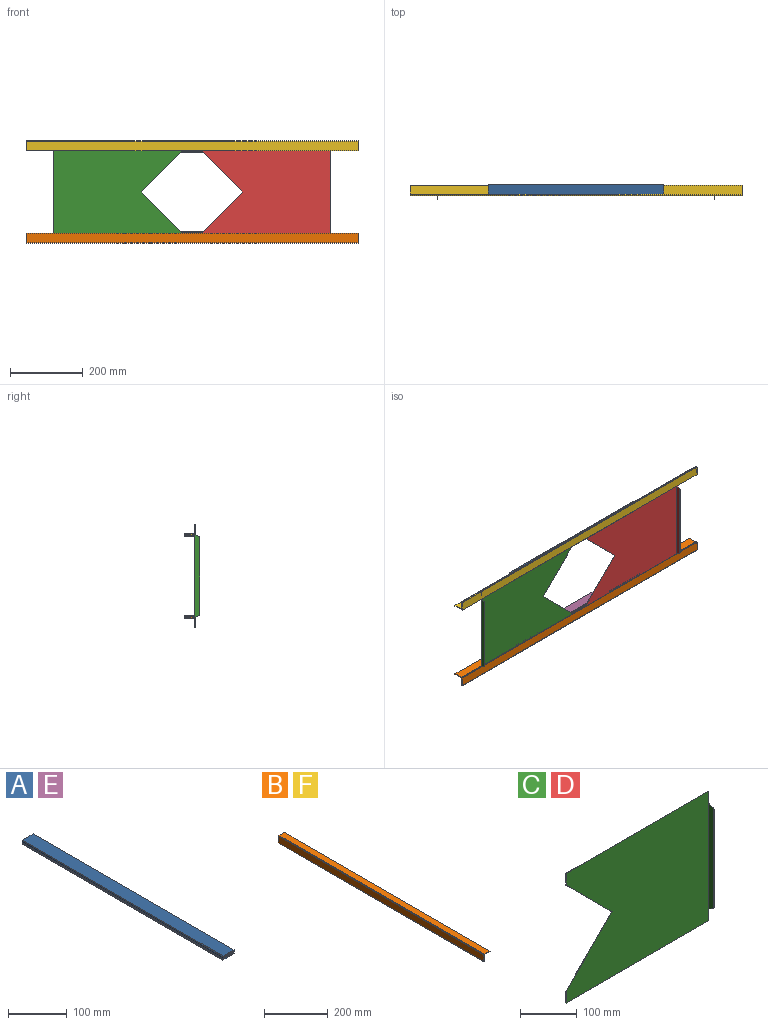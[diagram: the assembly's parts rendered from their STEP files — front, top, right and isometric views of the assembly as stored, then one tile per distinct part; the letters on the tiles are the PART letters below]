
ASSEMBLY  parts=6 mates=13
PART A: 18 faces, bbox 27x482.6x8 mm
  f0: plane 482.6x1.6mm, normal (-1,0,0), area 772.3mm2, adj f1,f11,f12,f13
  f1: plane 482.6x26.24mm, normal (0,0,-1), area 12662.6mm2, adj f0,f12,f13,f17
  f2: plane 482.6x3.28mm, normal (1,0,0), area 1581.3mm2, adj f12,f13,f16,f17
  f3: plane 482.6x24.64mm, normal (0,0,1), area 11890.3mm2, adj f4,f12,f13,f16
  f4: plane 482.6x1.6mm, normal (1,0,0), area 772.3mm2, adj f3,f5,f12,f13
  f5: plane 482.6x25.4mm, normal (0,0,-1), area 12258mm2, adj f4,f6,f12,f13
  f6: plane 482.6x1.6mm, normal (1,0,0), area 772.3mm2, adj f5,f7,f12,f13
  f7: plane 482.6x26.24mm, normal (0,0,1), area 12662.6mm2, adj f6,f12,f13,f14
  f8: plane 482.6x3.28mm, normal (-1,0,0), area 1581.3mm2, adj f12,f13,f14,f15
  f9: plane 482.6x24.64mm, normal (0,0,-1), area 11890.3mm2, adj f10,f12,f13,f15
  f10: plane 482.6x1.6mm, normal (-1,0,0), area 772.3mm2, adj f9,f11,f12,f13
  f11: plane 482.6x25.4mm, normal (0,0,1), area 12258mm2, adj f0,f10,f12,f13
  f12: plane 27x8mm, normal (0,-1,0), area 134.2mm2, adj f0,f1,f2,f3,f4,f5,f6,f7
  f13: plane 27x8mm, normal (0,1,0), area 134.2mm2, adj f0,f1,f2,f3,f4,f5,f6,f7
  f14: cylinder r=0.76mm len=482.6mm, axis (0,1,0), area 577.6mm2, adj f7,f8,f12,f13
  f15: cylinder r=0.76mm len=482.6mm, axis (0,1,0), area 577.6mm2, adj f8,f9,f12,f13
  f16: cylinder r=0.76mm len=482.6mm, axis (0,1,0), area 577.6mm2, adj f2,f3,f12,f13
  f17: cylinder r=0.76mm len=482.6mm, axis (0,1,0), area 577.6mm2, adj f1,f2,f12,f13
PART B: 15 faces, bbox 28.3x914.4x27 mm
  f0: plane 914.4x1.59mm, normal (1,0,0), area 1451.6mm2, adj f1,f9,f10,f11
  f1: plane 914.4x23.88mm, normal (0,0,1), area 21832.2mm2, adj f0,f10,f11,f14
  f2: plane 914.4x23.88mm, normal (-1,0,0), area 21832.2mm2, adj f3,f10,f11,f14
  f3: plane 914.4x1.27mm, normal (0,0,1), area 1161.3mm2, adj f2,f4,f10,f11
  f4: plane 914.4x25.4mm, normal (1,0,0), area 23225.8mm2, adj f3,f5,f10,f11
  f5: plane 914.4x1.59mm, normal (0,0,1), area 1451.6mm2, adj f4,f6,f10,f11
  f6: plane 914.4x25.46mm, normal (-1,0,0), area 23283.8mm2, adj f5,f10,f11,f13
  f7: plane 914.4x1.4mm, normal (0,0,-1), area 1277.4mm2, adj f10,f11,f12,f13
  f8: plane 914.4x23.88mm, normal (1,0,0), area 21832.2mm2, adj f9,f10,f11,f12
  f9: plane 914.4x23.81mm, normal (0,0,-1), area 21774.1mm2, adj f0,f8,f10,f11
  f10: plane 28.26x26.99mm, normal (0,-1,0), area 124mm2, adj f0,f1,f2,f3,f4,f5,f6,f7
  f11: plane 28.26x26.99mm, normal (0,1,0), area 124mm2, adj f0,f1,f2,f3,f4,f5,f6,f7
  f12: cylinder r=1.52mm len=914.4mm, axis (0,1,0), area 2189mm2, adj f7,f8,f10,f11
  f13: cylinder r=1.52mm len=914.4mm, axis (0,1,0), area 2189mm2, adj f6,f7,f10,f11
  f14: cylinder r=1.52mm len=914.4mm, axis (0,1,0), area 2189mm2, adj f1,f2,f10,f11
PART C: 16 faces, bbox 355.6x13.3x279.4 mm
  f0: plane 228.6x12.7mm, normal (1,0,0), area 2819.2mm2, adj f1,f11,f12,f13,f14,f15
  f1: plane 209.62x0.55mm, normal (0,-1,0), area 115.5mm2, adj f0,f2,f14,f15
  f2: plane 228.6x12.7mm, normal (-1,0,0), area 2819.2mm2, adj f1,f3,f12,f13,f14,f15
  f3: plane 355.6x279.4mm, normal (0,-1,0), area 86164.2mm2, adj f2,f4,f5,f6,f7,f8,f9,f11
  f4: plane 355.6x0.55mm, normal (0,0,-1), area 195.9mm2, adj f3,f9,f10,f11
  f5: plane 355.6x0.55mm, normal (0,0,1), area 195.9mm2, adj f3,f6,f10,f11
  f6: plane 25.4x0.55mm, normal (-1,0,0), area 14mm2, adj f3,f5,f7,f10
  f7: plane 114.3x114.3mm, normal (-0.71,0,-0.71), area 89.1mm2, adj f3,f6,f8,f10
  f8: plane 114.3x114.3mm, normal (-0.71,0,0.71), area 89.1mm2, adj f3,f7,f9,f10
  f9: plane 25.4x0.55mm, normal (-1,0,0), area 14mm2, adj f3,f4,f8,f10
  f10: plane 355.05x279.4mm, normal (0,1,0), area 86136.2mm2, adj f4,f5,f6,f7,f8,f9,f11
  f11: cylinder r=0.55mm len=279.4mm, axis (0,0,1), area 241.9mm2, adj f0,f3,f4,f5,f10
  f12: plane 9.89x4.95mm, normal (0,-0.45,-0.89), area 6.1mm2, adj f0,f2,f3,f15
  f13: plane 9.89x4.95mm, normal (0,-0.45,0.89), area 6.1mm2, adj f0,f2,f3,f14
  f14: cylinder r=5.08mm len=4.54mm, axis (-1,0,0), area 3.1mm2, adj f0,f1,f2,f13
  f15: cylinder r=5.08mm len=4.54mm, axis (1,0,0), area 3.1mm2, adj f0,f1,f2,f12
PART D: same geometry as C
PART E: same geometry as A
PART F: same geometry as B
PLACE A rot(axis=(0,0,-1),90deg) t=(-215.9,15.09,225.37)mm
PLACE B rot(axis=(0,0,1),90deg) t=(-914.4,-13.49,1.59)mm
PLACE C rot(axis=(0,1,0),180deg) t=(-482.6,-13.49,255.59)mm
PLACE D t=(-431.8,-13.49,-23.81)mm
PLACE E rot(axis=(0,0,1),90deg) t=(-699.3,-11.91,-1.6)mm
PLACE F rot(axis=(-0.71,-0.71,0),180deg) t=(0,-13.49,230.19)mm
MATE planar B.f3 <-> C.f5  axis (0,0,1) through (-457.2,-14.13,-23.81)mm
MATE planar E.f11 <-> B.f9  axis (0,0,1) through (-458,0.79,0)mm
MATE planar F.f8 <-> A.f6  axis (0,1,0) through (-457.2,-11.91,243.71)mm
MATE parallel F.f14 <-> D.f0  axis (1,0,0) through (0,-11.97,231.71)mm
MATE planar A.f5 <-> F.f9  axis (0,0,-1) through (-457.2,0.79,231.77)mm
MATE planar B.f3 <-> D.f4  axis (0,0,1) through (-457.2,-14.13,-23.81)mm
MATE planar B.f10 <-> F.f11  axis (1,0,0) through (0,-0.03,1.59)mm
MATE planar F.f3 <-> D.f5  axis (0,0,-1) through (-457.2,-14.13,255.59)mm
MATE planar E.f0 <-> B.f8  axis (0,-1,0) through (-458,-11.91,-0.8)mm
MATE planar B.f2 <-> D.f10  axis (0,-1,0) through (-457.2,-13.49,-11.87)mm
MATE planar C.f3 <-> D.f3  axis (0,-1,0) through (-681.32,-14.04,115.89)mm
MATE parallel B.f14 <-> C.f0  axis (-1,0,0) through (-914.4,-11.97,0.06)mm
MATE planar F.f6 <-> B.f6  axis (0,-1,0) through (-457.2,-16.35,242.92)mm
